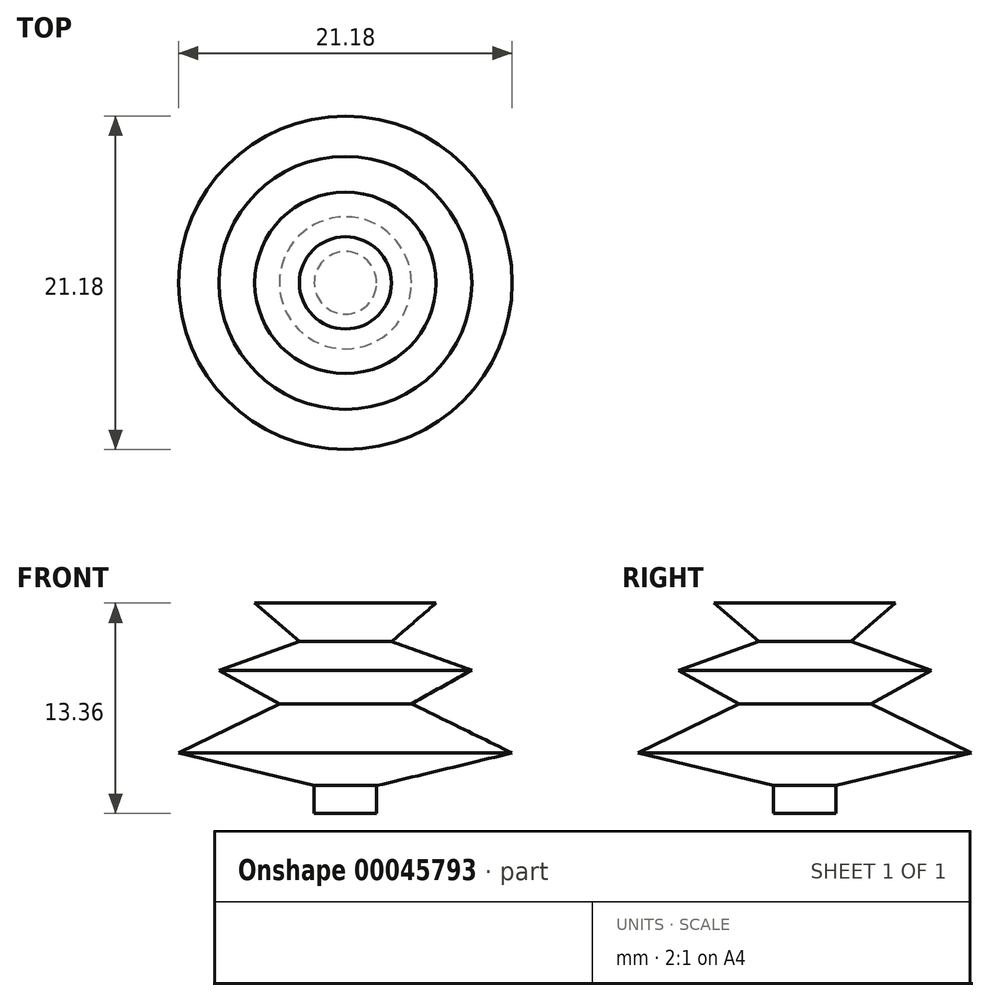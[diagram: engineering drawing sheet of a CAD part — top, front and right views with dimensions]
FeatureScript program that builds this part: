
annotation { "Feature Type Name" : "Feature", "Feature Type Description" : "" }
export const myFeature = defineFeature(function(context is Context, id is Id, definition is map)
    precondition{}
    {
        {
            var Q0;
            Q0=qCreatedBy(makeId("Front.planeOp"),FACE);
            var sketch = newSketch(context, id + "F0", { "sketchPlane" : qUnion([Q0])});
            skLineSegment(sketch, "E0", {"start": v(0, 0) * mm, "end": v(1.98, 0) * mm});
            skLineSegment(sketch, "E1", {"start": v(1.98, 0) * mm, "end": v(1.98, 1.77) * mm});
            skLineSegment(sketch, "E2", {"start": v(1.98, 1.77) * mm, "end": v(10.59, 3.84) * mm});
            skLineSegment(sketch, "E3", {"start": v(10.59, 3.84) * mm, "end": v(4.2, 6.96) * mm});
            skLineSegment(sketch, "E4", {"start": v(4.2, 6.96) * mm, "end": v(8.03, 9.1) * mm});
            skLineSegment(sketch, "E5", {"start": v(8.03, 9.1) * mm, "end": v(2.93, 10.9) * mm});
            skLineSegment(sketch, "E6", {"start": v(2.93, 10.9) * mm, "end": v(5.76, 13.36) * mm});
            skLineSegment(sketch, "E7", {"start": v(0, 20) * mm, "end": v(0, 0) * mm});
            skArc(sketch, "E8", {"start": v(0, 20) * mm, "mid": v(1.64, 15.6) * mm, "end": v(5.76, 13.36) * mm});
            skSolve(sketch);
        }
        {
            var Q0;
            Q0 = qSketchRegion(id + "F0", true);
            var Q1;
            Q1=sQuery(id+"F0.wireOp",EDGE,"E7");
            revolve(context, id + "F1", {"entities" : qUnion([Q0]), "axis" : qUnion([Q1]), "revolveType" : RevolveType.FULL});
        }
    });
